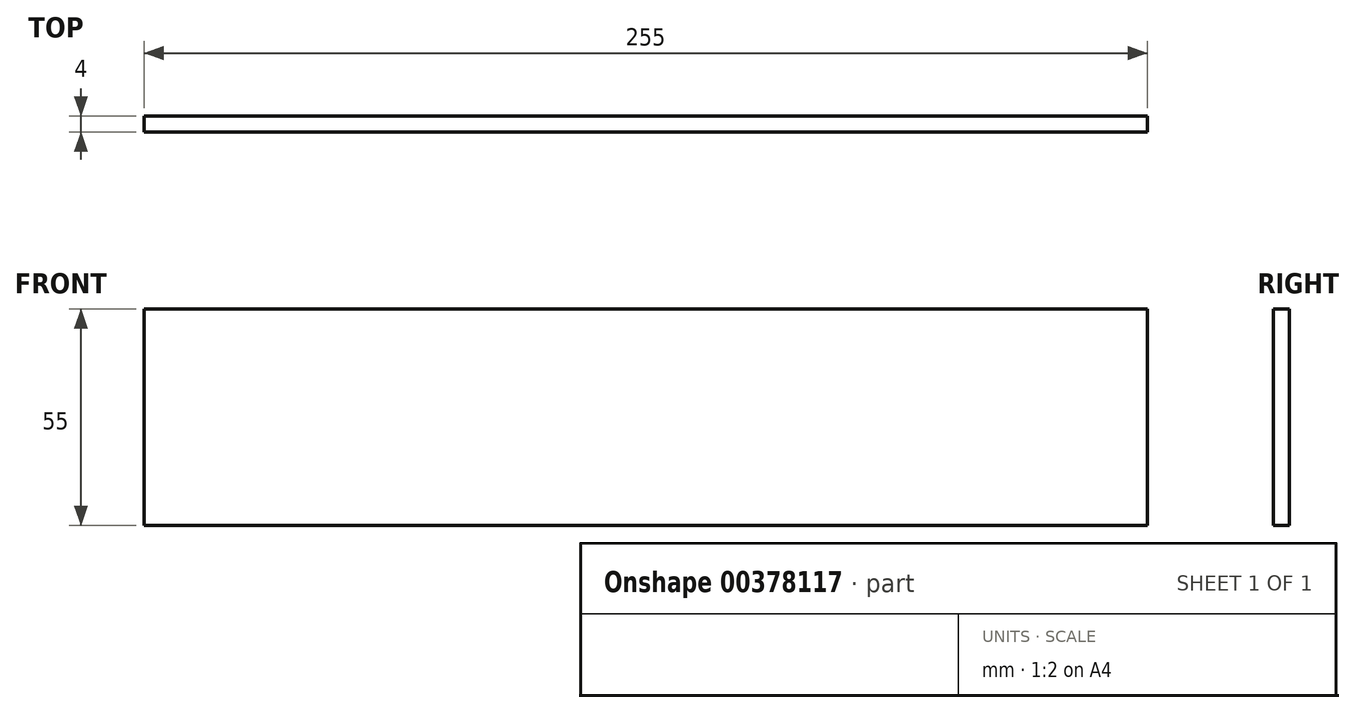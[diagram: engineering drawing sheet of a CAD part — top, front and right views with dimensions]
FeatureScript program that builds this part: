
annotation { "Feature Type Name" : "Feature", "Feature Type Description" : "" }
export const myFeature = defineFeature(function(context is Context, id is Id, definition is map)
    precondition{}
    {
        {
            var Q0;
            Q0=qCreatedBy(makeId("Front.planeOp"),FACE);
            var sketch = newSketch(context, id + "F0", { "sketchPlane" : qUnion([Q0])});
            skLineSegment(sketch, "E0.bottom", {"start": v(0, 0) * mm, "end": v(255, 0) * mm});
            skLineSegment(sketch, "E0.top", {"start": v(0, 55) * mm, "end": v(255, 55) * mm});
            skLineSegment(sketch, "E0.left", {"start": v(0, 0) * mm, "end": v(0, 55) * mm});
            skLineSegment(sketch, "E0.right", {"start": v(255, 0) * mm, "end": v(255, 55) * mm});
            skSolve(sketch);
        }
        {
            var Q0;
            Q0=makeQuery(id+"F0.imprint","IMPRINT",FACE,{"disambiguationData":[TD([[makeQuery(id+"F0.imprint","IMPRINT",EDGE,{"derivedFrom":sQuery(id+"F0.wireOp",EDGE,"E0.bottom")}),1.0]])]});
            extrude(context, id + "F1", {"entities" : qUnion([Q0]), "depth" : 4 * mm});
        }
    });
